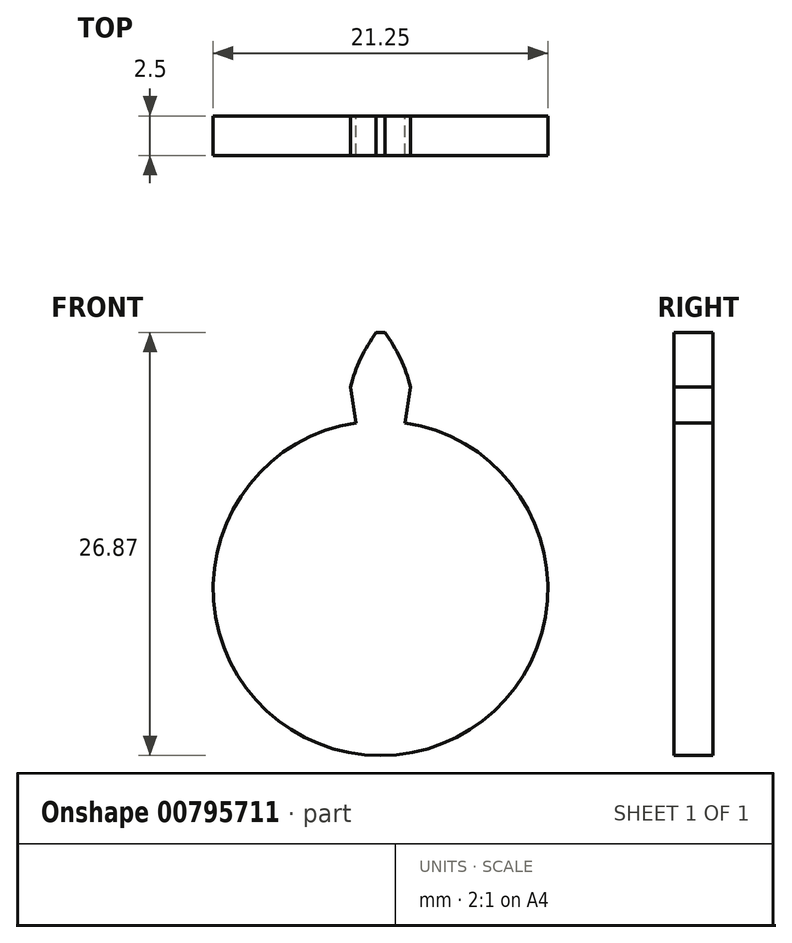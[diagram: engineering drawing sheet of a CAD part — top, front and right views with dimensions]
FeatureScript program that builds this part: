
annotation { "Feature Type Name" : "Feature", "Feature Type Description" : "" }
export const myFeature = defineFeature(function(context is Context, id is Id, definition is map)
    precondition{}
    {
        {
            assignVariable(context, id + "F0", {"name" : "m", "anyValue" : 2.5});
        }
        {
            var Q0;
            Q0=qCreatedBy(makeId("Front.planeOp"),FACE);
            var sketch = newSketch(context, id + "F1", { "sketchPlane" : qUnion([Q0])});
            skCircle(sketch, "E0", {"center": v(0, 0) * mm, "radius": 13.75 * mm, "construction": true});
            skArc(sketch, "E1.0", {"start": v(0.27, 16.25) * mm, "mid": v(0, 16.25) * mm, "end": v(-0.27, 16.25) * mm});
            skCircle(sketch, "E2.0", {"center": v(0, 0) * mm, "radius": 10.62 * mm});
            skArc(sketch, "E3", {"start": v(7.66, 10.4) * mm, "mid": v(3.11, 12.54) * mm, "end": v(-1.9, 12.78) * mm, "construction": true});
            skLineSegment(sketch, "E4", {"start": v(-0.27, 16.25) * mm, "end": v(7.66, 10.4) * mm, "construction": true});
            skLineSegment(sketch, "E5", {"start": v(0, 0) * mm, "end": v(4.3, 0) * mm});
            skLineSegment(sketch, "E6", {"start": v(7.66, 10.4) * mm, "end": v(0, 0) * mm, "construction": true});
            skLineSegment(sketch, "E7", {"start": v(0, 0) * mm, "end": v(-0.27, 16.25) * mm, "construction": true});
            skArc(sketch, "E8", {"start": v(-0.27, 16.25) * mm, "mid": v(-1.26, 14.6) * mm, "end": v(-1.9, 12.78) * mm});
            skLineSegment(sketch, "E9", {"start": v(0, 0) * mm, "end": v(0, 9.31) * mm});
            skLineSegment(sketch, "E10", {"start": v(-1.9, 12.78) * mm, "end": v(-1.57, 10.5) * mm});
            skArc(sketch, "E11.MirrorCS", {"start": v(0.27, 16.25) * mm, "mid": v(1.26, 14.6) * mm, "end": v(1.9, 12.78) * mm});
            skLineSegment(sketch, "E12.MirrorCS", {"start": v(1.9, 12.78) * mm, "end": v(1.57, 10.5) * mm});
            skSolve(sketch);
        }
        {
            var Q0;
            Q0=makeQuery(id+"F1.imprint","IMPRINT",FACE,{"disambiguationData":[TD([[makeQuery(id+"F1.imprint","IMPRINT",EDGE,{"derivedFrom":sQuery(id+"F1.wireOp",EDGE,"E1.0")}),1.0]])]});
            extrude(context, id + "F2", {"entities" : qUnion([Q0]), "depth" : (getVariable(context, 'm')) * mm, "offsetDistance" : 25 * mm});
        }
        {
            var Q0;
            {var subQ0=sQuery(id+"F1.wireOp",EDGE,"E2.0");var subQ1=makeQuery(id+"F1.imprint","INTERSECT",VERTEX,{"derivedFrom":[subQ0,sQuery(id+"F1.wireOp",EDGE,"E10")]});Q0=makeQuery(id+"F1.imprint","IMPRINT",FACE,{"disambiguationData":[TD([[makeQuery(id+"F1.imprint","IMPRINT",EDGE,{"disambiguationData":[TD([[subQ1,1.0]])],"derivedFrom":subQ0}),1.0]])]});}
            extrude(context, id + "F3", {"entities" : qUnion([Q0]), "operationType" : NewBodyOperationType.ADD, "depth" : (getVariable(context, 'm')) * mm, "offsetDistance" : 25 * mm});
        }
        {
            var Q0;
            Q0=qCreatedBy(makeId("Right.planeOp"),FACE);
            var sketch = newSketch(context, id + "F4", { "sketchPlane" : qUnion([Q0])});
            skLineSegment(sketch, "E13", {"start": v(0, 0) * mm, "end": v(-0.81, 0) * mm});
            skSolve(sketch);
        }
    });
